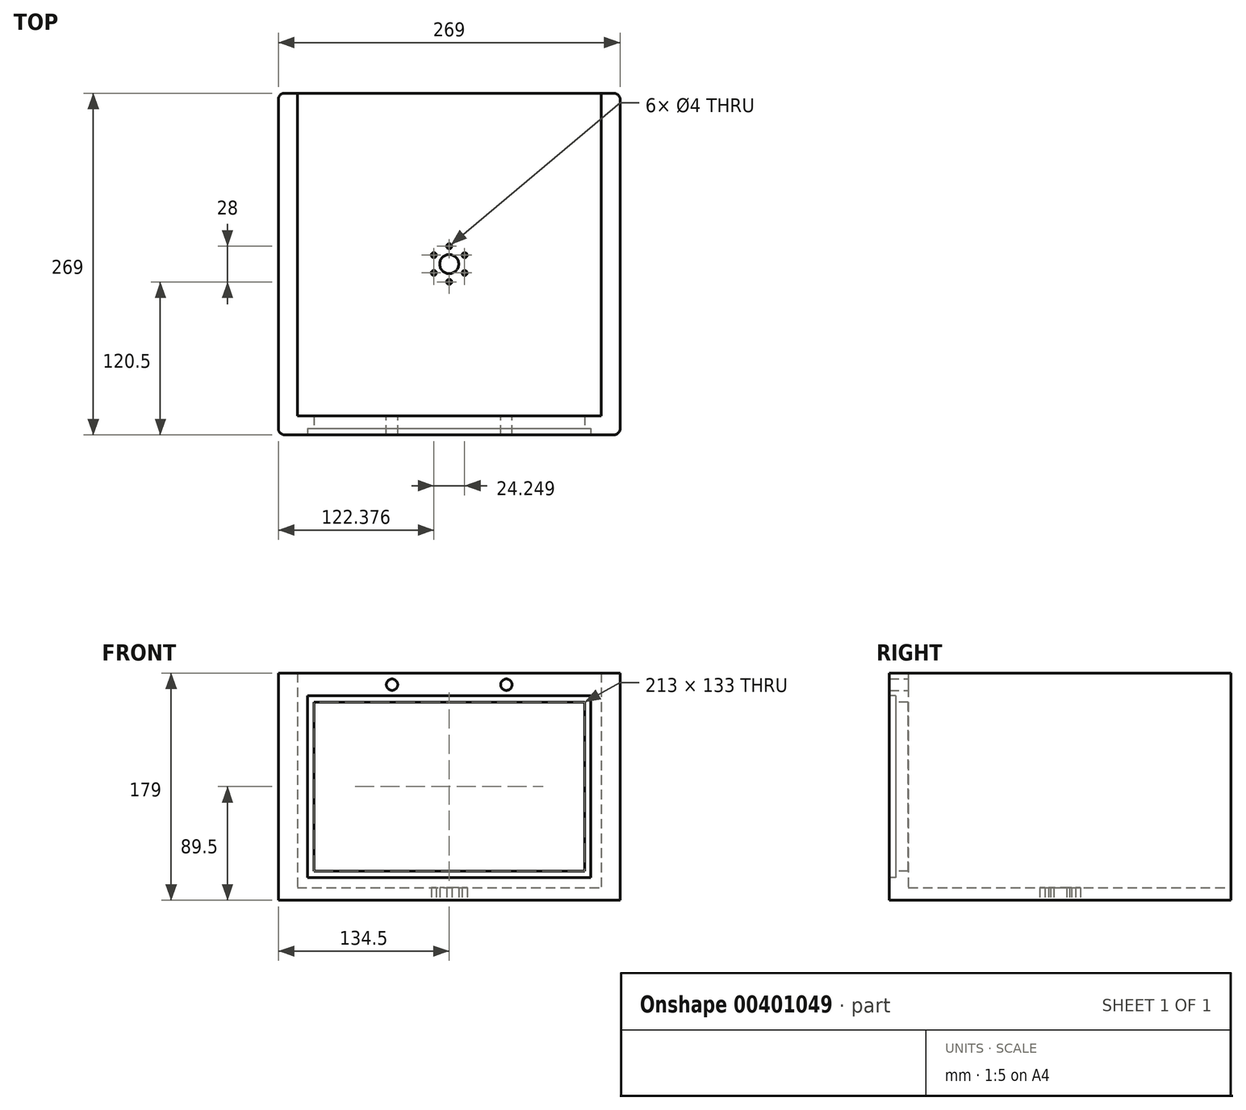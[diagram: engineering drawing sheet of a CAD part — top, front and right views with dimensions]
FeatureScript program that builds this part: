
annotation { "Feature Type Name" : "Feature", "Feature Type Description" : "" }
export const myFeature = defineFeature(function(context is Context, id is Id, definition is map)
    precondition{}
    {
        {
            var Q0;
            Q0=qCreatedBy(makeId("Top.planeOp"),FACE);
            var sketch = newSketch(context, id + "F0", { "sketchPlane" : qUnion([Q0])});
            skLineSegment(sketch, "E0.bottom", {"start": v(-129.5, 134.5) * mm, "end": v(129.5, 134.5) * mm});
            skLineSegment(sketch, "E0.top", {"start": v(-129.5, -134.5) * mm, "end": v(129.5, -134.5) * mm});
            skLineSegment(sketch, "E0.left", {"start": v(-134.5, 129.5) * mm, "end": v(-134.5, -129.5) * mm});
            skLineSegment(sketch, "E0.right", {"start": v(134.5, 129.5) * mm, "end": v(134.5, -129.5) * mm});
            skPoint(sketch, "E1.visualSharp", {"position": v(-134.5, 134.5) * mm});
            skArc(sketch, "E1.filletArc", {"start": v(-129.5, 134.5) * mm, "mid": v(-133.04, 133.04) * mm, "end": v(-134.5, 129.5) * mm});
            skPoint(sketch, "E2.visualSharp", {"position": v(-134.5, -134.5) * mm});
            skArc(sketch, "E2.filletArc", {"start": v(-134.5, -129.5) * mm, "mid": v(-133.04, -133.04) * mm, "end": v(-129.5, -134.5) * mm});
            skPoint(sketch, "E3.visualSharp", {"position": v(134.5, -134.5) * mm});
            skArc(sketch, "E3.filletArc", {"start": v(129.5, -134.5) * mm, "mid": v(133.04, -133.04) * mm, "end": v(134.5, -129.5) * mm});
            skPoint(sketch, "E4.visualSharp", {"position": v(134.5, 134.5) * mm});
            skArc(sketch, "E4.filletArc", {"start": v(134.5, 129.5) * mm, "mid": v(133.04, 133.04) * mm, "end": v(129.5, 134.5) * mm});
            skCircle(sketch, "E5", {"center": v(0, 0) * mm, "radius": 7.5 * mm});
            skCircle(sketch, "E6", {"center": v(0, 14) * mm, "radius": 2 * mm});
            skCircle(sketch, "E7.1.0", {"center": v(-12.12, 7) * mm, "radius": 2 * mm});
            skCircle(sketch, "E7.2.0", {"center": v(-12.12, -7) * mm, "radius": 2 * mm});
            skCircle(sketch, "E7.3.0", {"center": v(0, -14) * mm, "radius": 2 * mm});
            skCircle(sketch, "E7.4.0", {"center": v(12.12, -7) * mm, "radius": 2 * mm});
            skCircle(sketch, "E7.5.0", {"center": v(12.12, 7) * mm, "radius": 2 * mm});
            skSolve(sketch);
        }
        {
            var Q0;
            Q0=makeQuery(id+"F0.imprint","IMPRINT",FACE,{"disambiguationData":[TD([[makeQuery(id+"F0.imprint","IMPRINT",EDGE,{"derivedFrom":sQuery(id+"F0.wireOp",EDGE,"E0.bottom")}),-1.0]])]});
            extrude(context, id + "F1", {"entities" : qUnion([Q0]), "depth" : 10 * mm});
        }
        {
            var Q0;
            Q0=makeQuery(id+"F1.opExtrude","CAP_FACE",FACE,{"disambiguationData":[OSD([sQuery(id+"F0.wireOp",EDGE,"E0.bottom"),sQuery(id+"F0.wireOp",EDGE,"E0.top"),sQuery(id+"F0.wireOp",EDGE,"E0.left"),sQuery(id+"F0.wireOp",EDGE,"E0.right"),sQuery(id+"F0.wireOp",EDGE,"E1.filletArc"),sQuery(id+"F0.wireOp",EDGE,"E2.filletArc"),sQuery(id+"F0.wireOp",EDGE,"E3.filletArc"),sQuery(id+"F0.wireOp",EDGE,"E4.filletArc"),sQuery(id+"F0.wireOp",EDGE,"E5"),sQuery(id+"F0.wireOp",EDGE,"E6"),sQuery(id+"F0.wireOp",EDGE,"E7.1.0"),sQuery(id+"F0.wireOp",EDGE,"E7.2.0"),sQuery(id+"F0.wireOp",EDGE,"E7.3.0"),sQuery(id+"F0.wireOp",EDGE,"E7.4.0"),sQuery(id+"F0.wireOp",EDGE,"E7.5.0")])],"isStart":false});
            var sketch = newSketch(context, id + "F2", { "sketchPlane" : qUnion([Q0])});
            skLineSegment(sketch, "E8.bottom", {"start": v(-129.5, -134.5) * mm, "end": v(129.5, -134.5) * mm});
            skLineSegment(sketch, "E8.top", {"start": v(-119.5, -119.5) * mm, "end": v(119.5, -119.5) * mm});
            skLineSegment(sketch, "E8.left", {"start": v(-134.5, -129.5) * mm, "end": v(-134.5, -119.5) * mm});
            skLineSegment(sketch, "E8.right", {"start": v(134.5, -129.5) * mm, "end": v(134.5, -119.5) * mm});
            skPoint(sketch, "E9.visualSharp", {"position": v(134.5, -134.5) * mm});
            skArc(sketch, "E9.filletArc", {"start": v(129.5, -134.5) * mm, "mid": v(133.04, -133.04) * mm, "end": v(134.5, -129.5) * mm});
            skPoint(sketch, "E10.visualSharp", {"position": v(-134.5, -134.5) * mm});
            skArc(sketch, "E10.filletArc", {"start": v(-134.5, -129.5) * mm, "mid": v(-133.04, -133.04) * mm, "end": v(-129.5, -134.5) * mm});
            skLineSegment(sketch, "E11.top", {"start": v(-129.5, 134.5) * mm, "end": v(-119.5, 134.5) * mm});
            skLineSegment(sketch, "E11.left", {"start": v(-134.5, -119.5) * mm, "end": v(-134.5, 129.5) * mm});
            skLineSegment(sketch, "E11.right", {"start": v(-119.5, -119.5) * mm, "end": v(-119.5, 134.5) * mm});
            skLineSegment(sketch, "E12.top", {"start": v(129.5, 134.5) * mm, "end": v(119.5, 134.5) * mm});
            skLineSegment(sketch, "E12.left", {"start": v(134.5, -119.5) * mm, "end": v(134.5, 129.5) * mm});
            skLineSegment(sketch, "E12.right", {"start": v(119.5, -119.5) * mm, "end": v(119.5, 134.5) * mm});
            skPoint(sketch, "E13.visualSharp", {"position": v(-134.5, 134.5) * mm});
            skArc(sketch, "E13.filletArc", {"start": v(-129.5, 134.5) * mm, "mid": v(-133.04, 133.04) * mm, "end": v(-134.5, 129.5) * mm});
            skPoint(sketch, "E14.visualSharp", {"position": v(134.5, 134.5) * mm});
            skArc(sketch, "E14.filletArc", {"start": v(134.5, 129.5) * mm, "mid": v(133.04, 133.04) * mm, "end": v(129.5, 134.5) * mm});
            skSolve(sketch);
        }
        {
            var Q0;
            Q0=makeQuery(id+"F2.imprint","IMPRINT",FACE,{"disambiguationData":[TD([[makeQuery(id+"F2.imprint","IMPRINT",EDGE,{"derivedFrom":sQuery(id+"F2.wireOp",EDGE,"E8.bottom")}),1.0]])]});
            extrude(context, id + "F3", {"entities" : qUnion([Q0]), "operationType" : NewBodyOperationType.ADD, "depth" : 169 * mm});
        }
        {
            var Q0;
            Q0=makeQuery(id+"F3.boolean.opBoolean","MERGE",FACE,{"derivedFrom":[makeQuery(id+"F1.opExtrude","SWEPT_FACE",FACE,{"disambiguationData":[OSD([sQuery(id+"F0.wireOp",EDGE,"E0.top")])]}),makeQuery(id+"F3.opExtrude","SWEPT_FACE",FACE,{"disambiguationData":[OSD([sQuery(id+"F2.wireOp",EDGE,"E8.bottom")])]})]});
            var sketch = newSketch(context, id + "F4", { "sketchPlane" : qUnion([Q0])});
            skLineSegment(sketch, "E15.bottom", {"start": v(-111.5, 161) * mm, "end": v(111.5, 161) * mm});
            skLineSegment(sketch, "E15.top", {"start": v(-111.5, 18) * mm, "end": v(111.5, 18) * mm});
            skLineSegment(sketch, "E15.left", {"start": v(-111.5, 161) * mm, "end": v(-111.5, 18) * mm});
            skLineSegment(sketch, "E15.right", {"start": v(111.5, 161) * mm, "end": v(111.5, 18) * mm});
            skLineSegment(sketch, "E16.0", {"start": v(-106.5, 156) * mm, "end": v(-106.5, 23) * mm});
            skLineSegment(sketch, "E16.1", {"start": v(-106.5, 156) * mm, "end": v(106.5, 156) * mm});
            skLineSegment(sketch, "E16.2", {"start": v(106.5, 156) * mm, "end": v(106.5, 23) * mm});
            skLineSegment(sketch, "E16.3", {"start": v(-106.5, 23) * mm, "end": v(106.5, 23) * mm});
            skSolve(sketch);
        }
        {
            var Q0;
            Q0=makeQuery(id+"F4.imprint","IMPRINT",FACE,{"disambiguationData":[TD([[makeQuery(id+"F4.imprint","IMPRINT",EDGE,{"derivedFrom":sQuery(id+"F4.wireOp",EDGE,"E15.bottom")}),-1.0]])]});
            extrude(context, id + "F5", {"entities" : qUnion([Q0]), "operationType" : NewBodyOperationType.REMOVE, "oppositeDirection" : true, "depth" : 5 * mm});
        }
        {
            var Q0;
            Q0=makeQuery(id+"F5.boolean.opBoolean","SPLIT",FACE,{"disambiguationData":[TD([makeQuery(id+"F5.opExtrude","SWEPT_FACE",FACE,{"disambiguationData":[OSD([sQuery(id+"F4.wireOp",EDGE,"E16.0")])]})])],"derivedFrom":makeQuery(id+"F3.boolean.opBoolean","MERGE",FACE,{"derivedFrom":[makeQuery(id+"F1.opExtrude","SWEPT_FACE",FACE,{"disambiguationData":[OSD([sQuery(id+"F0.wireOp",EDGE,"E0.top")])]}),makeQuery(id+"F3.opExtrude","SWEPT_FACE",FACE,{"disambiguationData":[OSD([sQuery(id+"F2.wireOp",EDGE,"E8.bottom")])]})]})});
            extrude(context, id + "F6", {"entities" : qUnion([Q0]), "operationType" : NewBodyOperationType.REMOVE, "oppositeDirection" : true, "depth" : 25 * mm});
        }
        {
            var Q0;
            Q0=makeQuery(id+"F3.opExtrude","SWEPT_FACE",FACE,{"disambiguationData":[OSD([sQuery(id+"F2.wireOp",EDGE,"E8.top")])]});
            var sketch = newSketch(context, id + "F7", { "sketchPlane" : qUnion([Q0])});
            skCircle(sketch, "E17", {"center": v(-45, 169.8) * mm, "radius": 4.5 * mm});
            skCircle(sketch, "E18", {"center": v(45, 169.8) * mm, "radius": 4.5 * mm});
            skSolve(sketch);
        }
        {
            var Q0;
            Q0=makeQuery(id+"F7.imprint","IMPRINT",FACE,{"disambiguationData":[TD([[makeQuery(id+"F7.imprint","IMPRINT",EDGE,{"derivedFrom":sQuery(id+"F7.wireOp",EDGE,"E17")}),1.0]])]});
            var Q1;
            Q1=makeQuery(id+"F7.imprint","IMPRINT",FACE,{"disambiguationData":[TD([[makeQuery(id+"F7.imprint","IMPRINT",EDGE,{"derivedFrom":sQuery(id+"F7.wireOp",EDGE,"E18")}),1.0]])]});
            extrude(context, id + "F8", {"entities" : qUnion([Q0, Q1]), "operationType" : NewBodyOperationType.REMOVE, "oppositeDirection" : true, "depth" : 25 * mm});
        }
    });
